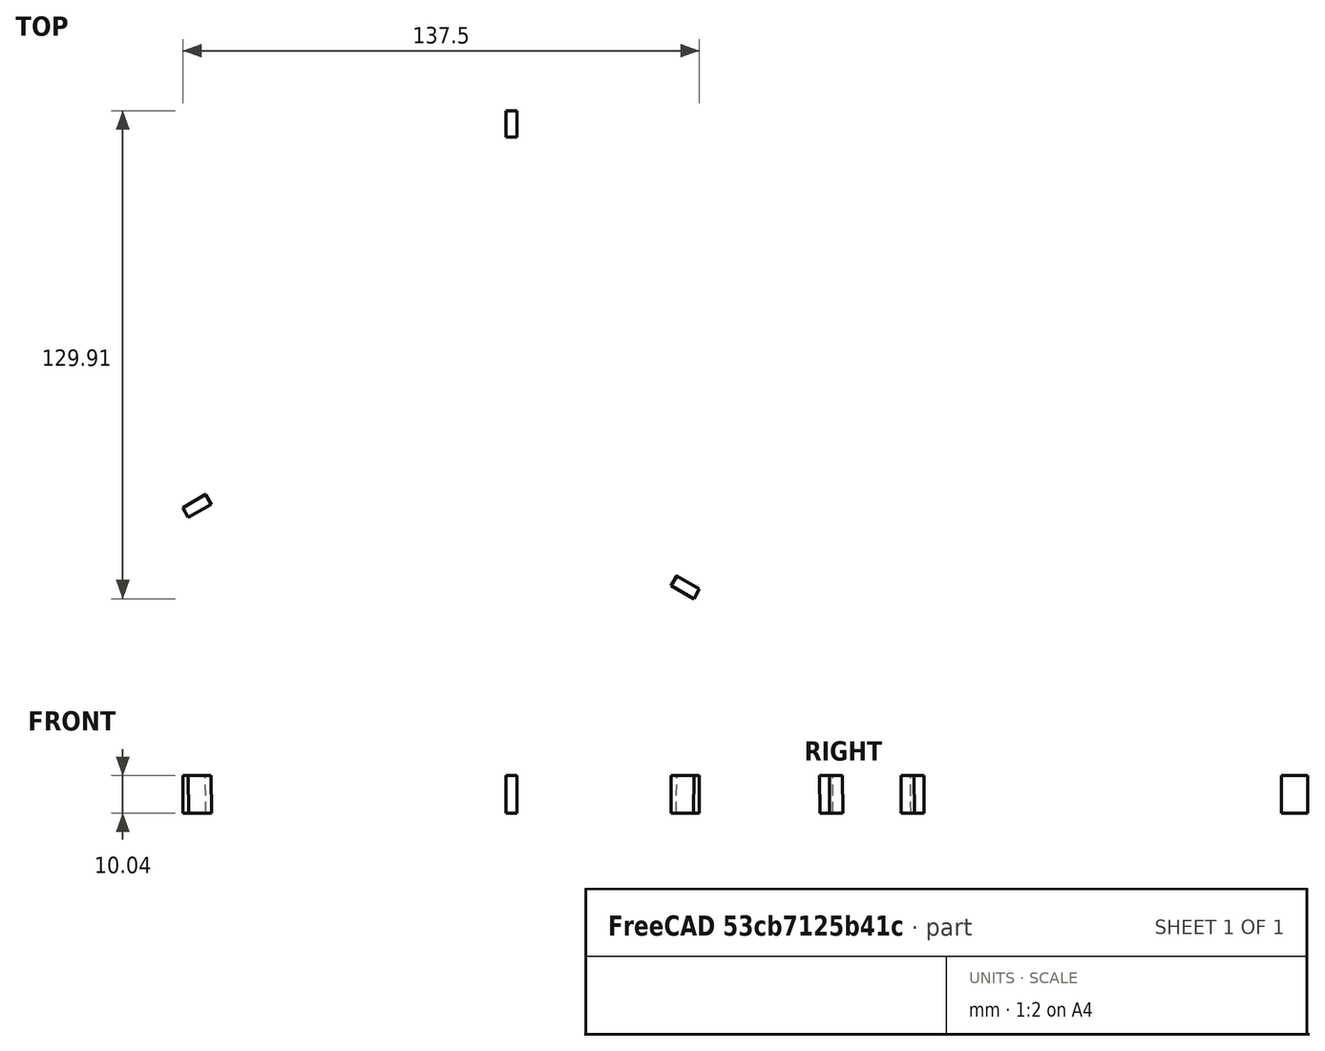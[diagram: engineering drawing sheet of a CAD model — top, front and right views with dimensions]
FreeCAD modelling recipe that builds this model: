
FCSTD DOCUMENT  (FreeCAD 2024.1R35694 (Git))
Label: deltarobot-example
License: All rights reserved
LicenseURL: http://en.wikipedia.org/wiki/All_rights_reserved
objects: App::FeaturePython×22, App::Link×17, Part::FeaturePython×3, Assembly::JointGroup×1, Assembly::AssemblyObject×1
note: 3 computed .brp shape members not serialized (recipe doc carries the construction recipe); baked Part::Feature solids carry a one-line shape summary decoded from their .brp
EXTERNAL_REF file=base.FCStd obj=Part
EXTERNAL_REF file=nema17-48.FCStd obj=Part
EXTERNAL_REF file=arm.FCStd obj=Part
EXTERNAL_REF file=plate.FCStd obj=Part
EXTERNAL_REF file=link.FCStd obj=Part
EXTERNAL_REF file=cone.FCStd obj=Part

FEATURE [App::Link] base  label="base 🔒"
  LinkedObject = -> <external base.FCStd>#Part
FEATURE [App::Link] nema17_48
  LinkPlacement = pos=(66.4519,-34.9019,1.93e-14) rot=(0.935113,-0.250563,-0.250563;1.63783rad)
  LinkedObject = -> <external nema17-48.FCStd>#Part
  Placement = pos=(66.4519,-34.9019,1.93e-14) rot=(0.935113,-0.250563,-0.250563;1.63783rad)
FEATURE [App::Link] nema17_049
  LinkPlacement = pos=(-63.4519,-40.0981,5.19e-14) rot=(-0.935113,-0.250563,0.250563;1.63783rad)
  LinkedObject = -> <external nema17-48.FCStd>#Part
  Placement = pos=(-63.4519,-40.0981,5.19e-14) rot=(-0.935113,-0.250563,0.250563;1.63783rad)
FEATURE [App::Link] nema17_050
  LinkPlacement = pos=(-3,75,4.4e-15) rot=(0.57735,-0.57735,0.57735;4.18879rad)
  LinkedObject = -> <external nema17-48.FCStd>#Part
  Placement = pos=(-3,75,4.4e-15) rot=(0.57735,-0.57735,0.57735;4.18879rad)
FEATURE [App::FeaturePython] GroundedJoint  # Assembly grounded joint (typed FeaturePython)
  ObjectToGround = -> base
FEATURE [App::FeaturePython] Fixed  # Assembly joint (typed FeaturePython)
  Detach1 = false
  Detach2 = false
  Distance = 0
  Element1 = Edge11
  Element2 = Edge27
  FirstPartConnected = false
  JointType = 0 (Fixed)
  Object1 = Body
  Object2 = Body002
  Offset = (0,0,0)
  Part1 = -> nema17_48
  Part2 = -> base
  Placement1 = pos=(0,0,48) rot=(0,0,1;0rad)
  Placement2 = pos=(67.4519,-33.1699,1.95e-14) rot=(0.935113,-0.250563,-0.250563;1.63783rad)
  Rotation = 0
  Vertex1 = Edge11
  Vertex2 = Edge27
FEATURE [App::FeaturePython] Fixed001  # Assembly joint (typed FeaturePython)
  Detach1 = false
  Detach2 = false
  Distance = 0
  Element1 = Edge11
  Element2 = Edge32
  FirstPartConnected = false
  JointType = 0 (Fixed)
  Object1 = Body
  Object2 = Body002
  Offset = (0,0,0)
  Part1 = -> nema17_049
  Part2 = -> base
  Placement1 = pos=(0,0,48) rot=(0,0,1;0rad)
  Placement2 = pos=(-62.4519,-41.8301,5.28e-14) rot=(-0.186157,0.694747,0.694747;3.50969rad)
  Rotation = 0
  Vertex1 = Edge11
  Vertex2 = Edge32
FEATURE [App::FeaturePython] Fixed002  # Assembly joint (typed FeaturePython)
  Detach1 = false
  Detach2 = false
  Distance = 0
  Element1 = Edge11
  Element2 = Edge12
  FirstPartConnected = false
  JointType = 0 (Fixed)
  Object1 = Body
  Object2 = Body002
  Offset = (0,0,0)
  Part1 = -> nema17_050
  Part2 = -> base
  Placement1 = pos=(0,0,48) rot=(0,0,1;0rad)
  Placement2 = pos=(-5,75,4.4e-15) rot=(0.57735,0.57735,0.57735;2.0944rad)
  Rotation = 0
  Vertex1 = Edge11
  Vertex2 = Edge12
FEATURE [App::Link] arm
  LinkPlacement = pos=(61.4519,-43.5622,1.88e-14) rot=(0.696382,-0.186595,0.69299;2.7744rad)
  LinkedObject = -> <external arm.FCStd>#Part
  Placement = pos=(61.4519,-43.5622,1.88e-14) rot=(0.696382,-0.186595,0.69299;2.7744rad)
FEATURE [App::Link] arm001
  LinkPlacement = pos=(-68.4519,-31.4378,4.74e-14) rot=(0.250639,-0.935398,0.249419;1.6424rad)
  LinkedObject = -> <external arm.FCStd>#Part
  Placement = pos=(-68.4519,-31.4378,4.74e-14) rot=(0.250639,-0.935398,0.249419;1.6424rad)
FEATURE [App::Link] arm002
  LinkPlacement = pos=(7,75,5.5e-15) rot=(0.578288,0.578288,0.575471;4.18597rad)
  LinkedObject = -> <external arm.FCStd>#Part
  Placement = pos=(7,75,5.5e-15) rot=(0.578288,0.578288,0.575471;4.18597rad)
FEATURE [App::FeaturePython] Revolute  # Assembly joint (typed FeaturePython)
  Detach1 = false
  Detach2 = false
  Distance = 0
  Element1 = Edge44
  Element2 = Edge38
  FirstPartConnected = true
  JointType = 1 (Revolute)
  Object1 = Body
  Object2 = Body001
  Offset = (0,0,0)
  Part1 = -> nema17_48
  Part2 = -> arm
  Placement1 = pos=(0,0,50) rot=(1,0,0;3.14159rad)
  Placement2 = pos=(0,-10,6.7e-15) rot=(1,0,0;1.5708rad)
  Rotation = 0
  Vertex1 = Edge44
  Vertex2 = Edge38
FEATURE [App::FeaturePython] Revolute001  # Assembly joint (typed FeaturePython)
  Detach1 = false
  Detach2 = false
  Distance = 0
  Element1 = Edge38
  Element2 = Edge44
  FirstPartConnected = false
  JointType = 1 (Revolute)
  Object1 = Body001
  Object2 = Body
  Offset = (0,0,0)
  Part1 = -> arm001
  Part2 = -> nema17_049
  Placement1 = pos=(0,-10,6.7e-15) rot=(1,0,0;1.5708rad)
  Placement2 = pos=(0,0,50) rot=(1,0,0;3.14159rad)
  Rotation = 0
  Vertex1 = Edge38
  Vertex2 = Edge44
FEATURE [App::FeaturePython] Revolute002  # Assembly joint (typed FeaturePython)
  Detach1 = false
  Detach2 = false
  Distance = 0
  Element1 = Edge38
  Element2 = Edge44
  FirstPartConnected = false
  JointType = 1 (Revolute)
  Object1 = Body001
  Object2 = Body
  Offset = (0,0,0)
  Part1 = -> arm002
  Part2 = -> nema17_050
  Placement1 = pos=(0,-10,6.7e-15) rot=(1,0,0;1.5708rad)
  Placement2 = pos=(0,0,50) rot=(1,0,0;3.14159rad)
  Rotation = 0
  Vertex1 = Edge38
  Vertex2 = Edge44
FEATURE [App::Link] plate
  LinkPlacement = pos=(8.1e-15,-1.46e-14,116) rot=(0,0,1;0rad)
  LinkedObject = -> <external plate.FCStd>#Part
  Placement = pos=(8.1e-15,-1.46e-14,116) rot=(0,0,1;0rad)
FEATURE [App::Link] link
  LinkPlacement = pos=(89.576,-22.8492,57.8706) rot=(-0.676617,0.713401,0.182342;1.52525rad)
  LinkedObject = -> <external link.FCStd>#Part
  Placement = pos=(89.576,-22.8492,57.8706) rot=(-0.676617,0.713401,0.182342;1.52525rad)
FEATURE [App::Link] link001
  LinkPlacement = pos=(64.576,-66.1505,57.8706) rot=(0.826476,0.110324,-0.552056;2.256rad)
  LinkedObject = -> <external link.FCStd>#Part
  Placement = pos=(64.576,-66.1505,57.8706) rot=(0.826476,0.110324,-0.552056;2.256rad)
FEATURE [App::Link] link002
  LinkPlacement = pos=(-64.576,-66.1505,57.8706) rot=(0.161974,0.81154,-0.561398;2.1205rad)
  LinkedObject = -> <external link.FCStd>#Part
  Placement = pos=(-64.576,-66.1505,57.8706) rot=(0.161974,0.81154,-0.561398;2.1205rad)
FEATURE [App::Link] link003
  LinkPlacement = pos=(-89.576,-22.8492,57.8706) rot=(-0.498673,0.455531,0.737439;2.90945rad)
  LinkedObject = -> <external link.FCStd>#Part
  Placement = pos=(-89.576,-22.8492,57.8706) rot=(-0.498673,0.455531,0.737439;2.90945rad)
FEATURE [App::Link] link004
  LinkPlacement = pos=(25,88.9997,57.8706) rot=(0.362835,0.914909,0.176894;1.72299rad)
  LinkedObject = -> <external link.FCStd>#Part
  Placement = pos=(25,88.9997,57.8706) rot=(0.362835,0.914909,0.176894;1.72299rad)
FEATURE [App::Link] link005
  LinkPlacement = pos=(-25,88.9997,57.8706) rot=(0.226144,-0.912799,-0.340083;1.62472rad)
  LinkedObject = -> <external link.FCStd>#Part
  Placement = pos=(-25,88.9997,57.8706) rot=(0.226144,-0.912799,-0.340083;1.62472rad)
FEATURE [App::FeaturePython] Ball  # Assembly joint (typed FeaturePython)
  Detach1 = false
  Detach2 = false
  Distance = 0
  Element1 = Face10
  Element2 = Face17
  FirstPartConnected = false
  JointType = 4 (Ball)
  Object1 = Body
  Object2 = Body001
  Offset = (0,0,0)
  Part1 = -> link
  Part2 = -> arm
  Placement1 = pos=(70,0,0) rot=(1,0,0;3.14159rad)
  Placement2 = pos=(0,-32,53) rot=(0.57735,0.57735,0.57735;4.18879rad)
  Rotation = 0
  Vertex1 = Face10
  Vertex2 = Face17
FEATURE [App::FeaturePython] Ball001  # Assembly joint (typed FeaturePython)
  Detach1 = false
  Detach2 = false
  Distance = 0
  Element1 = Face18
  Element2 = Face9
  FirstPartConnected = false
  JointType = 4 (Ball)
  Object1 = Body001
  Object2 = Body
  Offset = (0,0,0)
  Part1 = -> plate
  Part2 = -> link
  Placement1 = pos=(55.8013,-3.34936,0) rot=(0.935113,-0.250563,-0.250563;1.63783rad)
  Placement2 = pos=(-70,0,0) rot=(0,0,1;3.14159rad)
  Rotation = 0
  Vertex1 = Face18
  Vertex2 = Face9
FEATURE [App::FeaturePython] Ball002  # Assembly joint (typed FeaturePython)
  Detach1 = false
  Detach2 = false
  Distance = 0
  Element1 = Face18
  Element2 = Face10
  FirstPartConnected = true
  JointType = 4 (Ball)
  Object1 = Body001
  Object2 = Body
  Offset = (0,0,0)
  Part1 = -> arm
  Part2 = -> link001
  Placement1 = pos=(0,18,53) rot=(0.57735,0.57735,0.57735;4.18879rad)
  Placement2 = pos=(70,0,0) rot=(1,0,0;3.14159rad)
  Rotation = 0
  Vertex1 = Face18
  Vertex2 = Face10
FEATURE [App::FeaturePython] Ball003  # Assembly joint (typed FeaturePython)
  Detach1 = false
  Detach2 = false
  Distance = 0
  Element1 = Face9
  Element2 = Face17
  FirstPartConnected = true
  JointType = 4 (Ball)
  Object1 = Body
  Object2 = Body001
  Offset = (0,0,0)
  Part1 = -> link001
  Part2 = -> plate
  Placement1 = pos=(-70,0,0) rot=(0,0,1;3.14159rad)
  Placement2 = pos=(30.8013,-46.6506,0) rot=(0.935113,-0.250563,-0.250563;1.63783rad)
  Rotation = 0
  Vertex1 = Face9
  Vertex2 = Face17
FEATURE [App::FeaturePython] Ball004  # Assembly joint (typed FeaturePython)
  Detach1 = false
  Detach2 = false
  Distance = 0
  Element1 = Face17
  Element2 = Face10
  FirstPartConnected = true
  JointType = 4 (Ball)
  Object1 = Body001
  Object2 = Body
  Offset = (0,0,0)
  Part1 = -> arm001
  Part2 = -> link002
  Placement1 = pos=(0,-32,53) rot=(0.57735,0.57735,0.57735;4.18879rad)
  Placement2 = pos=(70,0,0) rot=(1,0,0;3.14159rad)
  Rotation = 0
  Vertex1 = Face17
  Vertex2 = Face10
FEATURE [App::FeaturePython] Ball005  # Assembly joint (typed FeaturePython)
  Detach1 = false
  Detach2 = false
  Distance = 0
  Element1 = Face18
  Element2 = Face10
  FirstPartConnected = true
  JointType = 4 (Ball)
  Object1 = Body001
  Object2 = Body
  Offset = (0,0,0)
  Part1 = -> arm001
  Part2 = -> link003
  Placement1 = pos=(0,18,53) rot=(0.57735,0.57735,0.57735;4.18879rad)
  Placement2 = pos=(70,0,0) rot=(1,0,0;3.14159rad)
  Rotation = 0
  Vertex1 = Face18
  Vertex2 = Face10
FEATURE [App::FeaturePython] Ball006  # Assembly joint (typed FeaturePython)
  Detach1 = false
  Detach2 = false
  Distance = 0
  Element1 = Face3
  Element2 = Face9
  FirstPartConnected = true
  JointType = 4 (Ball)
  Object1 = Body001
  Object2 = Body
  Offset = (0,0,0)
  Part1 = -> plate
  Part2 = -> link002
  Placement1 = pos=(-30.8013,-46.6506,0) rot=(-0.186157,0.694747,0.694747;3.50969rad)
  Placement2 = pos=(-70,0,0) rot=(0,0,1;3.14159rad)
  Rotation = 0
  Vertex1 = Face3
  Vertex2 = Face9
FEATURE [App::FeaturePython] Ball007  # Assembly joint (typed FeaturePython)
  Detach1 = false
  Detach2 = false
  Distance = 0
  Element1 = Face1
  Element2 = Face9
  FirstPartConnected = true
  JointType = 4 (Ball)
  Object1 = Body001
  Object2 = Body
  Offset = (0,0,0)
  Part1 = -> plate
  Part2 = -> link003
  Placement1 = pos=(-55.8013,-3.34936,0) rot=(-0.186157,0.694747,0.694747;3.50969rad)
  Placement2 = pos=(-70,0,0) rot=(0,0,1;3.14159rad)
  Rotation = 0
  Vertex1 = Face1
  Vertex2 = Face9
FEATURE [App::FeaturePython] Ball008  # Assembly joint (typed FeaturePython)
  Detach1 = false
  Detach2 = false
  Distance = 0
  Element1 = Face17
  Element2 = Face9
  FirstPartConnected = true
  JointType = 4 (Ball)
  Object1 = Body001
  Object2 = Body
  Offset = (0,0,0)
  Part1 = -> arm002
  Part2 = -> link005
  Placement1 = pos=(0,-32,53) rot=(0.57735,0.57735,0.57735;4.18879rad)
  Placement2 = pos=(-70,0,0) rot=(0,0,1;3.14159rad)
  Rotation = 0
  Vertex1 = Face17
  Vertex2 = Face9
FEATURE [App::FeaturePython] Ball009  # Assembly joint (typed FeaturePython)
  Detach1 = false
  Detach2 = false
  Distance = 0
  Element1 = Face16
  Element2 = Face10
  FirstPartConnected = true
  JointType = 4 (Ball)
  Object1 = Body001
  Object2 = Body
  Offset = (0,0,0)
  Part1 = -> plate
  Part2 = -> link005
  Placement1 = pos=(-25,50,0) rot=(0.57735,0.57735,0.57735;2.0944rad)
  Placement2 = pos=(70,0,0) rot=(1,0,0;3.14159rad)
  Rotation = 0
  Vertex1 = Face16
  Vertex2 = Face10
FEATURE [App::FeaturePython] Ball010  # Assembly joint (typed FeaturePython)
  Detach1 = false
  Detach2 = false
  Distance = 0
  Element1 = Face18
  Element2 = Face10
  FirstPartConnected = true
  JointType = 4 (Ball)
  Object1 = Body001
  Object2 = Body
  Offset = (0,0,0)
  Part1 = -> arm002
  Part2 = -> link004
  Placement1 = pos=(0,18,53) rot=(0.57735,0.57735,0.57735;4.18879rad)
  Placement2 = pos=(70,0,0) rot=(1,0,0;3.14159rad)
  Rotation = 0
  Vertex1 = Face18
  Vertex2 = Face10
FEATURE [App::FeaturePython] Ball011  # Assembly joint (typed FeaturePython)
  Detach1 = false
  Detach2 = false
  Distance = 0
  Element1 = Face15
  Element2 = Face9
  FirstPartConnected = true
  JointType = 4 (Ball)
  Object1 = Body001
  Object2 = Body
  Offset = (0,0,0)
  Part1 = -> plate
  Part2 = -> link004
  Placement1 = pos=(25,50,0) rot=(0.57735,0.57735,0.57735;2.0944rad)
  Placement2 = pos=(-70,0,0) rot=(0,0,1;3.14159rad)
  Rotation = 0
  Vertex1 = Face15
  Vertex2 = Face9
FEATURE [App::Link] cone
  LinkPlacement = pos=(7,107,-26) rot=(0,0,1;0rad)
  LinkedObject = -> <external cone.FCStd>#Part
  Placement = pos=(7,107,-26) rot=(0,0,1;0rad)
FEATURE [App::Link] cone001
  LinkPlacement = pos=(-96,-48,-26) rot=(0,0,1;0rad)
  LinkedObject = -> <external cone.FCStd>#Part
  Placement = pos=(-96,-48,-26) rot=(0,0,1;0rad)
FEATURE [App::Link] cone002
  LinkPlacement = pos=(92,-61,-26) rot=(0,0,1;0rad)
  LinkedObject = -> <external cone.FCStd>#Part
  Placement = pos=(92,-61,-26) rot=(0,0,1;0rad)
FEATURE [Part::FeaturePython] MotorObserver0  # WARN: FeaturePython — macro-defined, semantics opaque (R4)
  Enabled = true
  Placement = pos=(58.7019,-48.3253,1.82e-14) rot=(0.655971,0.376593,0.654125;3.86752rad)
  Reversed = true
  TransfAngle = 360
FEATURE [Part::FeaturePython] MotorObserver1  # WARN: FeaturePython — macro-defined, semantics opaque (R4)
  Enabled = true
  Placement = pos=(-71.2019,-26.6747,4.45e-14) rot=(0.653335,-0.379333,0.655179;2.42206rad)
  Reversed = true
  TransfAngle = 360
FEATURE [Part::FeaturePython] MotorObserver2  # WARN: FeaturePython — macro-defined, semantics opaque (R4)
  Enabled = true
  Placement = pos=(12.5,75,5.9e-15) rot=(-0.002441,-0.999994,0.002441;1.5708rad)
  Reversed = true
  TransfAngle = 360
FEATURE [App::FeaturePython] Fixed003  # Assembly joint (typed FeaturePython)
  Activated = true
  Detach1 = false
  Detach2 = false
  Distance = 0
  Element1 = Face6
  Element2 = Edge34
  JointType = 0 (Fixed)
  Object1 = MotorObserver0
  Object2 = Body001
  Offset = (0,0,0)
  Part1 = -> MotorObserver0
  Part2 = -> arm
  Placement1 = pos=(2e-16,0,1.5) rot=(0,0,1;0rad)
  Placement2 = pos=(0,4,-2.7e-15) rot=(1,0,0;1.5708rad)
  Rotation = 0
  Vertex1 = Face6
  Vertex2 = Edge34
FEATURE [App::FeaturePython] Fixed004  # Assembly joint (typed FeaturePython)
  Activated = true
  Detach1 = false
  Detach2 = false
  Distance = 0
  Element1 = Face6
  Element2 = Edge34
  JointType = 0 (Fixed)
  Object1 = MotorObserver1
  Object2 = Body001
  Offset = (0,0,0)
  Part1 = -> MotorObserver1
  Part2 = -> arm001
  Placement1 = pos=(3e-16,0,1.5) rot=(0,0,1;0rad)
  Placement2 = pos=(0,4,-2.7e-15) rot=(1,0,0;1.5708rad)
  Rotation = 0
  Vertex1 = Face6
  Vertex2 = Edge34
FEATURE [App::FeaturePython] Fixed005  # Assembly joint (typed FeaturePython)
  Activated = true
  Detach1 = false
  Detach2 = false
  Distance = 0
  Element1 = Face6
  Element2 = Edge34
  JointType = 0 (Fixed)
  Object1 = MotorObserver2
  Object2 = Body001
  Offset = (0,0,0)
  Part1 = -> MotorObserver2
  Part2 = -> arm002
  Placement1 = pos=(1e-16,0,1.5) rot=(0,0,1;0rad)
  Placement2 = pos=(0,4,-2.7e-15) rot=(1,0,0;1.5708rad)
  Rotation = 0
  Vertex1 = Face6
  Vertex2 = Edge34
FEATURE [Assembly::JointGroup] Joints
  Group = -> [GroundedJoint,Fixed,Fixed001,Fixed002,Revolute,Revolute001,Revolute002,Ball,Ball001,Ball002,Ball003,Ball004,Ball005,Ball006,Ball007,Ball008,Ball009,Ball010,Ball011,Fixed003,Fixed004,Fixed005]
FEATURE [Assembly::AssemblyObject] Assembly  label="deltabot"
  Group = -> [Joints,base,nema17_48,nema17_049,nema17_050,GroundedJoint,Fixed,Fixed001,Fixed002,arm,arm001,arm002,Revolute,Revolute001,Revolute002,plate,link,link001,link002,link003,link004,link005,Ball,Ball001,Ball002,Ball003,Ball004,Ball005,Ball006,Ball007,Ball008,Ball009,Ball010,Ball011,cone,cone001,cone002,MotorObserver0,MotorObserver1,MotorObserver2,Fixed003,Fixed004,Fixed005]
  Origin = -> Origin
  Type = Assembly

RESOLVED EXTERNAL PARTS (link-assembly join: the EXTERNAL_REF files above that resolve inside this repo's crawl, each included once):
---- part arm.FCStd = doc fcstd_cb6b5a2d1849 ----
FCSTD DOCUMENT  (FreeCAD 2024.1R35694 (Git))
Label: arm
License: All rights reserved
LicenseURL: http://en.wikipedia.org/wiki/All_rights_reserved
objects: Sketcher::SketchObject×11, PartDesign::Pad×6, PartDesign::Plane×2, PartDesign::Revolution×2, PartDesign::Mirrored×2, PartDesign::Body×2, PartDesign::Pocket×2, PartDesign::Chamfer×1, PartDesign::Hole×1, PartDesign::Fillet×1, App::Part×1
note: 43 computed .brp shape members not serialized (recipe doc carries the construction recipe); baked Part::Feature solids carry a one-line shape summary decoded from their .brp

FEATURE [PartDesign::Plane] DatumPlane002  label="midplane001"
  AttachmentOffset = pos=(0,0,7) rot=(0,0,1;0rad)
  Length = 60
  MapMode = 5
  Placement = pos=(0,-7,1.6e-15) rot=(1,0,0;1.5708rad)
  ResizeMode = 0
  Support = -> [XZ_Plane002]
  Width = 60
FEATURE [Sketcher::SketchObject] Sketch008
  FullyConstrained = true
  MapMode = 5
  Placement = pos=(0,0,0) rot=(1,0,0;1.5708rad)
  Support = -> [XZ_Plane002]
  sketch-geometry (5):
    g0: Circle CenterX=0 CenterY=0 CenterZ=0 NormalX=0 NormalY=0 NormalZ=1 AngleXU=0 Radius=2.5
    g1: ArcOfCircle CenterX=0 CenterY=0 CenterZ=0 NormalX=0 NormalY=0 NormalZ=1 AngleXU=0 Radius=6 StartAngle=3.14159 EndAngle=6.28319
    g2: LineSegment StartX=-6 StartY=-1.9e-15 StartZ=0 EndX=-6 EndY=50 EndZ=0
    g3: LineSegment StartX=6 StartY=-1.5e-15 StartZ=0 EndX=6 EndY=50 EndZ=0
    g4: LineSegment StartX=-6 StartY=50 StartZ=0 EndX=6 EndY=50 EndZ=0
  constraints (12):
    c: Coincident(g0,g-1)
    c: Tangent(g1,g2) = 1.5708
    c: Tangent(g1,g3) = -1.5708
    c: Vertical(g3)
    c: Diameter(g0) = 5
    c: Distance(g1,g1) = 12
    c: PointOnObject(g1,g-1)
    c: Coincident(g4,g2)
    c: Coincident(g4,g3)
    c: DistanceY(g3,g3) = 50
    c: Vertical(g2)
    c: Symmetric(g2,g3,g-2)
FEATURE [PartDesign::Pad] Pad003
  Direction = (0,-1,2e-16)
  Length = 8
  Length2 = 10
  Midplane = true
  Placement = pos=(0,0,0) rot=(1,0,0;1.5708rad)
  Profile = -> Sketch008
  ReferenceAxis = -> Sketch008 [N_Axis]
  Type = 0
FEATURE [Sketcher::SketchObject] Sketch009
  FullyConstrained = true
  MapMode = 5
  Placement = pos=(0,0,0) rot=(1,0,0;1.5708rad)
  Support = -> [XZ_Plane002]
  sketch-geometry (2):
    g0: Circle CenterX=0 CenterY=0 CenterZ=0 NormalX=0 NormalY=0 NormalZ=1 AngleXU=0 Radius=2.5
    g1: Circle CenterX=0 CenterY=0 CenterZ=0 NormalX=0 NormalY=0 NormalZ=1 AngleXU=0 Radius=6
  constraints (4):
    c: Coincident(g0,g-1)
    c: Coincident(g1,g0)
    c: Diameter(g0) = 5
    c: Diameter(g1) = 12
FEATURE [PartDesign::Pad] Pad004
  BaseFeature = -> Pad003
  Direction = (0,-1,2e-16)
  Length = 10
  Length2 = 10
  Placement = pos=(0,0,0) rot=(1,0,0;1.5708rad)
  Profile = -> Sketch009
  ReferenceAxis = -> Sketch009 [N_Axis]
  Refine = true
  Type = 0
FEATURE [Sketcher::SketchObject] Sketch010
  ExternalGeometry = -> [Pad004]
  FullyConstrained = true
  MapMode = 5
  Placement = pos=(0,-7,1.6e-15) rot=(1,0,0;1.5708rad)
  Support = -> [DatumPlane002]
  sketch-geometry (4):
    g0: LineSegment StartX=-6 StartY=50 StartZ=0 EndX=6 EndY=50 EndZ=0
    g1: LineSegment StartX=6 StartY=50 StartZ=0 EndX=6 EndY=56 EndZ=0
    g2: LineSegment StartX=6 StartY=56 StartZ=0 EndX=-6 EndY=56 EndZ=0
    g3: LineSegment StartX=-6 StartY=56 StartZ=0 EndX=-6 EndY=50 EndZ=0
  constraints (10):
    c: Coincident(g0,g1)
    c: Coincident(g1,g2)
    c: Coincident(g2,g3)
    c: Coincident(g3,g0)
    c: Horizontal(g2)
    c: Vertical(g1)
    c: Vertical(g3)
    c: Coincident(g0,g-3)
    c: Coincident(g0,g-3)
    c: DistanceY(g1,g1) = 6
FEATURE [PartDesign::Pad] Pad005
  BaseFeature = -> Pad004
  Direction = (0,-1,2e-16)
  Length = 36
  Length2 = 10
  Midplane = true
  Placement = pos=(0,0,0) rot=(1,0,0;1.5708rad)
  Profile = -> Sketch010
  ReferenceAxis = -> Sketch010 [N_Axis]
  Refine = true
  Type = 0
FEATURE [Sketcher::SketchObject] Sketch011
  ExternalGeometry = -> [Pad005,DatumPlane002]
  FullyConstrained = true
  MapMode = 5
  Placement = pos=(0,0,0) rot=(0.57735,0.57735,0.57735;2.0944rad)
  Support = -> [YZ_Plane002]
  sketch-geometry (4):
    g0: LineSegment StartX=-37 StartY=53 StartZ=0 EndX=-25 EndY=53 EndZ=0
    g1: ArcOfCircle CenterX=-32 CenterY=53 CenterZ=0 NormalX=0 NormalY=0 NormalZ=1 AngleXU=0 Radius=5 StartAngle=0.643501 EndAngle=3.14159
    g2: LineSegment StartX=-28 StartY=56 StartZ=0 EndX=-25 EndY=56 EndZ=0
    g3: LineSegment StartX=-25 StartY=56 StartZ=0 EndX=-25 EndY=53 EndZ=0
  constraints (12):
    c: Symmetric(g-3,g-3,g0)
    c: PointOnObject(g1,g0)
    c: Coincident(g1,g0)
    c: PointOnObject(g0,g-3)
    c: Radius(g1) = 5
    c: Distance(g1,g-4) = 25
    c: Coincident(g1,g2)
    c: PointOnObject(g2,g-3)
    c: Horizontal(g2)
    c: Coincident(g2,g3)
    c: Coincident(g3,g0)
    c: DistanceY(g0,g2) = 3
FEATURE [PartDesign::Revolution] Revolution
  Angle = 360
  Angle2 = 60
  Axis = (0,1,0)
  Base = (0,-37,53)
  BaseFeature = -> Pad005
  Placement = pos=(0,0,0) rot=(1,0,0;1.5708rad)
  Profile = -> Sketch011
  ReferenceAxis = -> Sketch011 [Edge1]
  Refine = true
  Type = 0
FEATURE [PartDesign::Mirrored] Mirrored002
  BaseFeature = -> Revolution
  MirrorPlane = -> DatumPlane002
  Originals = -> [Revolution]
  Placement = pos=(0,0,0) rot=(1,0,0;1.5708rad)
  Refine = true
FEATURE [PartDesign::Body] Body001  label="arm-skeleton"
  Group = -> [Sketch008,Pad003,Sketch009,Pad004,DatumPlane002,Sketch010,Pad005,Sketch011,Revolution,Mirrored002]
  Origin = -> Origin002
  Tip = -> Mirrored002
FEATURE [PartDesign::Plane] DatumPlane003  label="midplane002"
  AttachmentOffset = pos=(0,0,7) rot=(0,0,1;0rad)
  Length = 60
  MapMode = 5
  Placement = pos=(0,-7,1.6e-15) rot=(1,0,0;1.5708rad)
  ResizeMode = 0
  Support = -> [XZ_Plane002]
  Width = 60
FEATURE [Sketcher::SketchObject] Sketch012
  FullyConstrained = true
  MapMode = 5
  Placement = pos=(0,0,0) rot=(1,0,0;1.5708rad)
  Support = -> [XZ_Plane003]
  sketch-geometry (5):
    g0: Circle CenterX=0 CenterY=0 CenterZ=0 NormalX=0 NormalY=0 NormalZ=1 AngleXU=0 Radius=2.5
    g1: ArcOfCircle CenterX=0 CenterY=0 CenterZ=0 NormalX=0 NormalY=0 NormalZ=1 AngleXU=0 Radius=6 StartAngle=3.14159 EndAngle=6.28319
    g2: LineSegment StartX=-6 StartY=-1.9e-15 StartZ=0 EndX=-6 EndY=50 EndZ=0
    g3: LineSegment StartX=6 StartY=-1.5e-15 StartZ=0 EndX=6 EndY=50 EndZ=0
    g4: LineSegment StartX=-6 StartY=50 StartZ=0 EndX=6 EndY=50 EndZ=0
  constraints (12):
    c: Coincident(g0,g-1)
    c: Tangent(g1,g2) = 1.5708
    c: Tangent(g1,g3) = -1.5708
    c: Vertical(g3)
    c: Diameter(g0) = 5
    c: Distance(g1,g1) = 12
    c: PointOnObject(g1,g-1)
    c: Coincident(g4,g2)
    c: Coincident(g4,g3)
    c: DistanceY(g3,g3) = 50
    c: Vertical(g2)
    c: Symmetric(g2,g3,g-2)
FEATURE [PartDesign::Pad] Pad006
  Direction = (0,-1,2e-16)
  Length = 8
  Length2 = 10
  Midplane = true
  Placement = pos=(0,0,0) rot=(1,0,0;1.5708rad)
  Profile = -> Sketch012
  ReferenceAxis = -> Sketch012 [N_Axis]
  Type = 0
FEATURE [Sketcher::SketchObject] Sketch013
  FullyConstrained = true
  MapMode = 5
  Placement = pos=(0,0,0) rot=(1,0,0;1.5708rad)
  Support = -> [XZ_Plane003]
  sketch-geometry (2):
    g0: Circle CenterX=0 CenterY=0 CenterZ=0 NormalX=0 NormalY=0 NormalZ=1 AngleXU=0 Radius=2.5
    g1: Circle CenterX=0 CenterY=0 CenterZ=0 NormalX=0 NormalY=0 NormalZ=1 AngleXU=0 Radius=6
  constraints (4):
    c: Coincident(g0,g-1)
    c: Coincident(g1,g0)
    c: Diameter(g0) = 5
    c: Diameter(g1) = 12
FEATURE [PartDesign::Pad] Pad007
  BaseFeature = -> Pad006
  Direction = (0,-1,2e-16)
  Length = 10
  Length2 = 10
  Placement = pos=(0,0,0) rot=(1,0,0;1.5708rad)
  Profile = -> Sketch013
  ReferenceAxis = -> Sketch013 [N_Axis]
  Refine = true
  Type = 0
FEATURE [Sketcher::SketchObject] Sketch014
  ExternalGeometry = -> [Pad007]
  FullyConstrained = true
  MapMode = 5
  Placement = pos=(0,-7,1.6e-15) rot=(1,0,0;1.5708rad)
  Support = -> [DatumPlane003]
  sketch-geometry (4):
    g0: LineSegment StartX=-6 StartY=50 StartZ=0 EndX=6 EndY=50 EndZ=0
    g1: LineSegment StartX=6 StartY=50 StartZ=0 EndX=6 EndY=56 EndZ=0
    g2: LineSegment StartX=6 StartY=56 StartZ=0 EndX=-6 EndY=56 EndZ=0
    g3: LineSegment StartX=-6 StartY=56 StartZ=0 EndX=-6 EndY=50 EndZ=0
  constraints (10):
    c: Coincident(g0,g1)
    c: Coincident(g1,g2)
    c: Coincident(g2,g3)
    c: Coincident(g3,g0)
    c: Horizontal(g2)
    c: Vertical(g1)
    c: Vertical(g3)
    c: Coincident(g0,g-3)
    c: Coincident(g0,g-3)
    c: DistanceY(g1,g1) = 6
FEATURE [PartDesign::Pad] Pad008
  BaseFeature = -> Pad007
  Direction = (0,-1,2e-16)
  Length = 36
  Length2 = 10
  Midplane = true
  Placement = pos=(0,0,0) rot=(1,0,0;1.5708rad)
  Profile = -> Sketch014
  ReferenceAxis = -> Sketch014 [N_Axis]
  Refine = true
  Type = 0
FEATURE [Sketcher::SketchObject] Sketch015
  ExternalGeometry = -> [Pad008,DatumPlane003]
  FullyConstrained = true
  MapMode = 5
  Placement = pos=(0,0,0) rot=(0.57735,0.57735,0.57735;2.0944rad)
  Support = -> [YZ_Plane003]
  sketch-geometry (4):
    g0: LineSegment StartX=-36.9 StartY=53 StartZ=0 EndX=-25 EndY=53 EndZ=0
    g1: ArcOfCircle CenterX=-32 CenterY=53 CenterZ=0 NormalX=0 NormalY=0 NormalZ=1 AngleXU=0 Radius=4.9 StartAngle=0.658897 EndAngle=3.14159
    g2: LineSegment StartX=-28.1257 StartY=56 StartZ=0 EndX=-25 EndY=56 EndZ=0
    g3: LineSegment StartX=-25 StartY=56 StartZ=0 EndX=-25 EndY=53 EndZ=0
  constraints (12):
    c: Symmetric(g-3,g-3,g0)
    c: PointOnObject(g1,g0)
    c: Coincident(g1,g0)
    c: PointOnObject(g0,g-3)
    c: Radius(g1) = 4.9
    c: Distance(g1,g-4) = 25
    c: Coincident(g1,g2)
    c: PointOnObject(g2,g-3)
    c: Horizontal(g2)
    c: Coincident(g2,g3)
    c: Coincident(g3,g0)
    c: DistanceY(g0,g2) = 3
FEATURE [PartDesign::Revolution] Revolution001
  Angle = 360
  Angle2 = 60
  Axis = (0,1,0)
  Base = (0,-36.9,53)
  BaseFeature = -> Pad008
  Placement = pos=(0,0,0) rot=(1,0,0;1.5708rad)
  Profile = -> Sketch015
  ReferenceAxis = -> Sketch015 [Edge1]
  Refine = true
  Type = 0
FEATURE [PartDesign::Mirrored] Mirrored003
  BaseFeature = -> Revolution001
  MirrorPlane = -> DatumPlane003
  Originals = -> [Revolution001]
  Placement = pos=(0,0,0) rot=(1,0,0;1.5708rad)
  Refine = true
FEATURE [PartDesign::Chamfer] Chamfer
  Angle = 45
  Base = -> Mirrored003 [Edge12,Edge10,Edge17,Edge21]
  BaseFeature = -> Mirrored003
  ChamferType = 0
  FlipDirection = false
  Placement = pos=(0,0,0) rot=(1,0,0;1.5708rad)
  Refine = true
  Size = 2
  Size2 = 1
  SupportTransform = false
  UseAllEdges = false
FEATURE [Sketcher::SketchObject] Sketch
  FullyConstrained = true
  MapMode = 5
  Placement = pos=(0,0,0) rot=(1,0,0;1.5708rad)
  Support = -> [XZ_Plane003]
  sketch-geometry (4):
    g0: LineSegment StartX=0.5 StartY=0 StartZ=0 EndX=0.5 EndY=10 EndZ=0
    g1: LineSegment StartX=0.5 StartY=10 StartZ=0 EndX=-0.5 EndY=10 EndZ=0
    g2: LineSegment StartX=-0.5 StartY=10 StartZ=0 EndX=-0.5 EndY=0 EndZ=0
    g3: LineSegment StartX=-0.5 StartY=0 StartZ=0 EndX=0.5 EndY=0 EndZ=0
  constraints (11):
    c: Coincident(g0,g1)
    c: Coincident(g1,g2)
    c: Coincident(g2,g3)
    c: Coincident(g3,g0)
    c: Vertical(g0)
    c: Vertical(g2)
    c: Horizontal(g1)
    c: Horizontal(g3)
    c: Symmetric(g2,g0,g-1)
    c: Distance(g1,g1) = 1
    c: DistanceY(g0,g0) = 10
FEATURE [PartDesign::Pocket] Pocket
  BaseFeature = -> Chamfer
  Direction = (0,1,-2e-16)
  Length = 5
  Length2 = 5
  Midplane = true
  Placement = pos=(0,0,0) rot=(1,0,0;1.5708rad)
  Profile = -> Sketch
  ReferenceAxis = -> Sketch [N_Axis]
  Refine = true
  Type = 1
FEATURE [Sketcher::SketchObject] Sketch016
  FullyConstrained = true
  MapMode = 5
  Placement = pos=(6,0,0) rot=(0.707107,0,0.707107;3.14159rad)
  Support = -> [Pocket]
  sketch-geometry (1):
    g0: Circle CenterX=5 CenterY=0 CenterZ=0 NormalX=0 NormalY=0 NormalZ=1 AngleXU=0 Radius=1.5
  constraints (3):
    c: PointOnObject(g0,g-1)
    c: Diameter(g0) = 3
    c: DistanceX(g-1,g0) = 5
FEATURE [PartDesign::Hole] Hole
  BaseFeature = -> Pocket
  CustomThreadClearance = 0
  Depth = 178.805
  DepthType = 1
  Diameter = 3.4
  DrillForDepth = false
  DrillPoint = 1
  DrillPointAngle = 118
  HoleCutCountersinkAngle = 90
  HoleCutCustomValues = false
  HoleCutDepth = 0
  HoleCutDiameter = 6.1
  HoleCutType = 0
  ModelThread = false
  Placement = pos=(0,0,0) rot=(1,0,0;1.5708rad)
  Profile = -> Sketch016
  Refine = true
  Tapered = false
  TaperedAngle = 90
  ThreadClass = 0
  ThreadDepth = 178.805
  ThreadDepthType = 0
  ThreadDirection = 0
  ThreadFit = 0
  ThreadSize = 9
  ThreadType = 1
  Threaded = false
  UseCustomThreadClearance = false
FEATURE [Sketcher::SketchObject] Sketch017
  ExternalGeometry = -> [Hole]
  FullyConstrained = true
  MapMode = 5
  Placement = pos=(-6,0,0) rot=(0.707107,0,-0.707107;3.14159rad)
  Support = -> [Hole]
  sketch-geometry (7):
    g0: LineSegment StartX=-1.5359 StartY=-4e-16 StartZ=0 EndX=-3.26795 EndY=3 EndZ=0
    g1: LineSegment StartX=-3.26795 StartY=3 StartZ=0 EndX=-6.73205 EndY=3 EndZ=0
    g2: LineSegment StartX=-6.73205 StartY=3 StartZ=0 EndX=-8.4641 EndY=-9e-16 EndZ=0
    g3: LineSegment StartX=-8.4641 StartY=-9e-16 StartZ=0 EndX=-6.73205 EndY=-3 EndZ=0
    g4: LineSegment StartX=-6.73205 StartY=-3 StartZ=0 EndX=-3.26795 EndY=-3 EndZ=0
    g5: LineSegment StartX=-3.26795 StartY=-3 StartZ=0 EndX=-1.5359 EndY=-4e-16 EndZ=0
    g6: Circle CenterX=-5 CenterY=-6e-16 CenterZ=0 NormalX=0 NormalY=0 NormalZ=1 AngleXU=0 Radius=3.4641
  constraints (16):
    c: Coincident(g0,g1)
    c: Coincident(g1,g2)
    c: Coincident(g2,g3)
    c: Coincident(g3,g4)
    c: Coincident(g4,g5)
    c: Coincident(g5,g0)
    c: Equal(g0, g1-g5) x5
    c: PointOnObject(g0,g6)
    c: PointOnObject(g1,g6)
    c: PointOnObject(g2,g6)
    c: PointOnObject(g3,g6)
    c: PointOnObject(g4,g6)
    c: PointOnObject(g5,g6)
    c: Coincident(g6,g-3)
    c: DistanceY(g4,g0) = 6
    c: Horizontal(g1)
FEATURE [PartDesign::Pocket] Pocket001
  BaseFeature = -> Hole
  Direction = (1,0,2e-16)
  Length = 3
  Length2 = 5
  Placement = pos=(0,0,0) rot=(1,0,0;1.5708rad)
  Profile = -> Sketch017
  ReferenceAxis = -> Sketch017 [N_Axis]
  Refine = true
  Type = 0
FEATURE [PartDesign::Fillet] Fillet
  Base = -> Pocket001 [Edge3,Edge46]
  BaseFeature = -> Pocket001
  Placement = pos=(0,0,0) rot=(1,0,0;1.5708rad)
  Radius = 2
  Refine = true
  SupportTransform = false
  UseAllEdges = false
FEATURE [PartDesign::Body] Body002  label="arm0"
  Group = -> [Sketch012,Pad006,Sketch013,Pad007,DatumPlane003,Sketch014,Pad008,Sketch015,Revolution001,Mirrored003,Chamfer,Sketch,Pocket,Sketch016,Hole,Sketch017,Pocket001,Fillet]
  Origin = -> Origin003
  Tip = -> Fillet
FEATURE [App::Part] Part  label="arm"
  Group = -> [Body001,Body002]
  Origin = -> Origin
---- part base.FCStd = doc fcstd_4bb8bb395458 ----
FCSTD DOCUMENT  (FreeCAD 0.22R35451 (Git))
Label: base
License: All rights reserved
LicenseURL: http://en.wikipedia.org/wiki/All_rights_reserved
objects: Sketcher::SketchObject×7, PartDesign::Pad×5, PartDesign::Plane×4, PartDesign::PolarPattern×3, PartDesign::Body×2, PartDesign::Hole×1, PartDesign::Pocket×1, App::Part×1
note: 30 computed .brp shape members not serialized (recipe doc carries the construction recipe); baked Part::Feature solids carry a one-line shape summary decoded from their .brp

FEATURE [PartDesign::Plane] DatumPlane
  Length = 60
  MapMode = 5
  Placement = pos=(0,0,0) rot=(0.57735,0.57735,0.57735;2.0944rad)
  ResizeMode = 0
  Support = -> [YZ_Plane002]
  Width = 60
FEATURE [Sketcher::SketchObject] Sketch001
  FullyConstrained = true
  MapMode = 5
  Placement = pos=(0,0,0) rot=(0.57735,0.57735,0.57735;2.0944rad)
  Support = -> [DatumPlane]
  sketch-geometry (5):
    g0: Circle CenterX=75 CenterY=0 CenterZ=0 NormalX=0 NormalY=0 NormalZ=1 AngleXU=0 Radius=11.25
    g1: LineSegment StartX=96 StartY=21 StartZ=0 EndX=0 EndY=21 EndZ=0
    g2: LineSegment StartX=0 StartY=21 StartZ=0 EndX=0 EndY=-26 EndZ=0
    g3: LineSegment StartX=0 StartY=-26 StartZ=0 EndX=96 EndY=-26 EndZ=0
    g4: LineSegment StartX=96 StartY=-26 StartZ=0 EndX=96 EndY=21 EndZ=0
  constraints (15):
    c: PointOnObject(g0,g-1)
    c: Diameter(g0) = 22.5
    c: DistanceX(g-1,g0) = 75
    c: Coincident(g1,g2)
    c: Coincident(g2,g3)
    c: Coincident(g3,g4)
    c: Coincident(g4,g1)
    c: Horizontal(g1)
    c: Horizontal(g3)
    c: Vertical(g2)
    c: PointOnObject(g2,g-2)
    c: DistanceX(g0,g1) = 21
    c: DistanceY(g-1,g1) = 21
    c: DistanceY(g3,g-1) = 26
    c: Vertical(g4)
FEATURE [PartDesign::Pad] Pad001
  Direction = (1,0,0)
  Length = 5
  Length2 = 10
  Placement = pos=(0,0,0) rot=(0.57735,0.57735,0.57735;2.0944rad)
  Profile = -> Sketch001
  ReferenceAxis = -> Sketch001 [N_Axis]
  Reversed = true
  Type = 0
FEATURE [Sketcher::SketchObject] Sketch002
  ExternalGeometry = -> [Pad001]
  FullyConstrained = true
  MapMode = 5
  Placement = pos=(0,0,0) rot=(0.57735,0.57735,0.57735;2.0944rad)
  Support = -> [Pad001]
  sketch-geometry (5):
    g0: Circle CenterX=90.5 CenterY=15.5 CenterZ=0 NormalX=0 NormalY=0 NormalZ=1 AngleXU=0 Radius=2
    g1: LineSegment StartX=75 StartY=0 StartZ=0 EndX=75 EndY=11.25 EndZ=0
    g2: Circle CenterX=90.5 CenterY=-15.5 CenterZ=0 NormalX=0 NormalY=0 NormalZ=1 AngleXU=0 Radius=2
    g3: Circle CenterX=59.5 CenterY=-15.5 CenterZ=0 NormalX=0 NormalY=0 NormalZ=1 AngleXU=0 Radius=2
    g4: Circle CenterX=59.5 CenterY=15.5 CenterZ=0 NormalX=0 NormalY=0 NormalZ=1 AngleXU=0 Radius=2
  constraints (12):
    c: Coincident(g1,g-3)
    c: PointOnObject(g1,g-3)
    c: Vertical(g1)
    c: Symmetric(g0,g4,g1)
    c: Symmetric(g0,g2,g-1)
    c: Symmetric(g2,g3,g1)
    c: Equal(g4,g0)
    c: Equal(g0,g2)
    c: Equal(g2,g3)
    c: DistanceX(g4,g0) = 31
    c: DistanceY(g2,g0) = 31
    c: Diameter(g0) = 4
FEATURE [PartDesign::Hole] Hole
  BaseFeature = -> Pad001
  CustomThreadClearance = 0
  Depth = 25
  DepthType = 0
  Diameter = 3.4
  DrillForDepth = false
  DrillPoint = 1
  DrillPointAngle = 118
  HoleCutCountersinkAngle = 90
  HoleCutCustomValues = false
  HoleCutDepth = 3.4
  HoleCutDiameter = 6.1
  HoleCutType = 1
  ModelThread = false
  Placement = pos=(0,0,0) rot=(0.57735,0.57735,0.57735;2.0944rad)
  Profile = -> Sketch002
  Tapered = false
  TaperedAngle = 90
  ThreadClass = 0
  ThreadDepth = 25
  ThreadDepthType = 0
  ThreadDirection = 0
  ThreadFit = 0
  ThreadSize = 9
  ThreadType = 1
  Threaded = false
  UseCustomThreadClearance = false
FEATURE [PartDesign::Plane] DatumPlane001
  Length = 60
  MapMode = 5
  Placement = pos=(2.9e-15,0,-26) rot=(0.707107,0.707107,0;3.14159rad)
  ResizeMode = 0
  Support = -> [Pad001]
  Width = 60
FEATURE [Sketcher::SketchObject] Sketch003
  FullyConstrained = true
  MapMode = 5
  Placement = pos=(2.9e-15,0,-26) rot=(0.707107,0.707107,0;3.14159rad)
  Support = -> [DatumPlane001]
  sketch-geometry (1):
    g0: Circle CenterX=0 CenterY=0 CenterZ=0 NormalX=0 NormalY=0 NormalZ=1 AngleXU=0 Radius=5
  constraints (2):
    c: Coincident(g0,g-1)
    c: Diameter(g0) = 10
FEATURE [PartDesign::Pad] Pad002
  BaseFeature = -> Hole
  Direction = (0,0,-1)
  Length = 42
  Length2 = 10
  Placement = pos=(0,0,0) rot=(0.57735,0.57735,0.57735;2.0944rad)
  Profile = -> Sketch003
  ReferenceAxis = -> Sketch003 [N_Axis]
  Refine = true
  Reversed = true
  Type = 1
FEATURE [PartDesign::PolarPattern] PolarPattern
  Angle = 360
  Axis = -> Z_Axis002
  BaseFeature = -> Pad002
  Mode = 0
  Occurrences = 3
  Offset = 120
  Originals = -> [Pad001,Hole]
  Placement = pos=(0,0,0) rot=(0.57735,0.57735,0.57735;2.0944rad)
  Refine = true
FEATURE [Sketcher::SketchObject] Sketch
  FullyConstrained = true
  MapMode = 5
  Placement = pos=(2.9e-15,0,-26) rot=(0.707107,0.707107,0;3.14159rad)
  Support = -> [DatumPlane001]
  sketch-geometry (8):
    g0: LineSegment StartX=96 StartY=0 StartZ=0 EndX=-48 EndY=83.1384 EndZ=0
    g1: LineSegment StartX=-48 StartY=83.1384 StartZ=0 EndX=-48 EndY=-83.1384 EndZ=0
    g2: LineSegment StartX=-48 StartY=-83.1384 StartZ=0 EndX=96 EndY=0 EndZ=0
    g3: Circle CenterX=0 CenterY=0 CenterZ=0 NormalX=0 NormalY=0 NormalZ=1 AngleXU=0 Radius=96
    g4: LineSegment StartX=60 StartY=0 StartZ=0 EndX=-30 EndY=51.9615 EndZ=0
    g5: LineSegment StartX=-30 StartY=51.9615 StartZ=0 EndX=-30 EndY=-51.9615 EndZ=0
    g6: LineSegment StartX=-30 StartY=-51.9615 StartZ=0 EndX=60 EndY=0 EndZ=0
    g7: Circle CenterX=0 CenterY=0 CenterZ=0 NormalX=0 NormalY=0 NormalZ=1 AngleXU=0 Radius=60
  constraints (22):
    c: Coincident(g0,g1)
    c: Coincident(g1,g2)
    c: Coincident(g2,g0)
    c: Equal(g0,g1)
    c: Equal(g0,g2)
    c: PointOnObject(g0,g3)
    c: PointOnObject(g1,g3)
    c: PointOnObject(g2,g3)
    c: Coincident(g3,g-1)
    c: PointOnObject(g2,g-1)
    c: Coincident(g4,g5)
    c: Coincident(g5,g6)
    c: Coincident(g6,g4)
    c: Equal(g4,g5)
    c: Equal(g4,g6)
    c: PointOnObject(g4,g7)
    c: PointOnObject(g5,g7)
    c: PointOnObject(g6,g7)
    c: Coincident(g7,g3)
    c: PointOnObject(g6,g-1)
    c: DistanceX(g-1,g0) = 96
    c: DistanceX(g-1,g4) = 60
FEATURE [PartDesign::Pad] Pad
  BaseFeature = -> PolarPattern
  Direction = (0,0,-1)
  Length = 4
  Length2 = 10
  Placement = pos=(0,0,0) rot=(0.57735,0.57735,0.57735;2.0944rad)
  Profile = -> Sketch
  ReferenceAxis = -> Sketch [N_Axis]
  Refine = true
  Reversed = true
  Type = 0
FEATURE [Sketcher::SketchObject] Sketch004
  ExternalGeometry = -> [Pad]
  FullyConstrained = true
  MapMode = 5
  Placement = pos=(0,0,0) rot=(0.57735,0.57735,0.57735;2.0944rad)
  Support = -> [YZ_Plane002]
  sketch-geometry (4):
    g0: LineSegment StartX=82 StartY=21 StartZ=0 EndX=68 EndY=21 EndZ=0
    g1: LineSegment StartX=68 StartY=21 StartZ=0 EndX=68 EndY=8.80696 EndZ=0
    g2: LineSegment StartX=68 StartY=8.80696 StartZ=0 EndX=82 EndY=8.80696 EndZ=0
    g3: LineSegment StartX=82 StartY=8.80696 StartZ=0 EndX=82 EndY=21 EndZ=0
  constraints (12):
    c: Coincident(g0,g1)
    c: Coincident(g1,g2)
    c: Coincident(g2,g3)
    c: Coincident(g3,g0)
    c: Horizontal(g0)
    c: Horizontal(g2)
    c: Vertical(g1)
    c: Vertical(g3)
    c: PointOnObject(g0,g-4)
    c: PointOnObject(g1,g-3)
    c: PointOnObject(g2,g-3)
    c: DistanceX(g0,g0) = 14
FEATURE [PartDesign::Pocket] Pocket
  BaseFeature = -> Pad
  Direction = (-1,0,0)
  Length = 5
  Length2 = 5
  Placement = pos=(0,0,0) rot=(0.57735,0.57735,0.57735;2.0944rad)
  Profile = -> Sketch004
  ReferenceAxis = -> Sketch004 [N_Axis]
  Refine = true
  Type = 0
FEATURE [PartDesign::PolarPattern] PolarPattern001
  Angle = 360
  Axis = -> Z_Axis002
  BaseFeature = -> Pocket
  Mode = 0
  Occurrences = 3
  Offset = 120
  Originals = -> [Pocket]
  Placement = pos=(0,0,0) rot=(0.57735,0.57735,0.57735;2.0944rad)
  Refine = true
FEATURE [PartDesign::Body] Body001  label="base0"
  Group = -> [DatumPlane,Sketch001,Pad001,DatumPlane001,Sketch002,Hole,Sketch003,Pad002,PolarPattern,Sketch,Pad,Sketch004,Pocket,PolarPattern001]
  Origin = -> Origin002
  Tip = -> PolarPattern001
FEATURE [PartDesign::Plane] DatumPlane002
  Length = 60
  MapMode = 5
  Placement = pos=(0,0,0) rot=(0.57735,0.57735,0.57735;2.0944rad)
  ResizeMode = 0
  Support = -> [YZ_Plane003]
  Width = 60
FEATURE [Sketcher::SketchObject] Sketch006
  FullyConstrained = true
  MapMode = 5
  Placement = pos=(0,0,0) rot=(0.57735,0.57735,0.57735;2.0944rad)
  Support = -> [DatumPlane002]
  sketch-geometry (5):
    g0: Circle CenterX=75 CenterY=0 CenterZ=0 NormalX=0 NormalY=0 NormalZ=1 AngleXU=0 Radius=11.25
    g1: LineSegment StartX=96 StartY=21 StartZ=0 EndX=0 EndY=21 EndZ=0
    g2: LineSegment StartX=0 StartY=21 StartZ=0 EndX=0 EndY=-26 EndZ=0
    g3: LineSegment StartX=0 StartY=-26 StartZ=0 EndX=96 EndY=-26 EndZ=0
    g4: LineSegment StartX=96 StartY=-26 StartZ=0 EndX=96 EndY=21 EndZ=0
  constraints (15):
    c: PointOnObject(g0,g-1)
    c: Diameter(g0) = 22.5
    c: DistanceX(g-1,g0) = 75
    c: Coincident(g1,g2)
    c: Coincident(g2,g3)
    c: Coincident(g3,g4)
    c: Coincident(g4,g1)
    c: Horizontal(g1)
    c: Horizontal(g3)
    c: Vertical(g2)
    c: PointOnObject(g2,g-2)
    c: DistanceX(g0,g1) = 21
    c: DistanceY(g-1,g1) = 21
    c: DistanceY(g3,g-1) = 26
    c: Vertical(g4)
FEATURE [PartDesign::Pad] Pad004
  Direction = (1,0,0)
  Length = 5
  Length2 = 10
  Placement = pos=(0,0,0) rot=(0.57735,0.57735,0.57735;2.0944rad)
  Profile = -> Sketch006
  ReferenceAxis = -> Sketch006 [N_Axis]
  Reversed = true
  Type = 0
FEATURE [PartDesign::Plane] DatumPlane003
  Length = 60
  MapMode = 5
  Placement = pos=(2.9e-15,0,-26) rot=(0.707107,0.707107,0;3.14159rad)
  ResizeMode = 0
  Support = -> [Pad004]
  Width = 60
FEATURE [Sketcher::SketchObject] Sketch008
  FullyConstrained = true
  MapMode = 5
  Placement = pos=(2.9e-15,0,-26) rot=(0.707107,0.707107,0;3.14159rad)
  Support = -> [DatumPlane003]
  sketch-geometry (1):
    g0: Circle CenterX=0 CenterY=0 CenterZ=0 NormalX=0 NormalY=0 NormalZ=1 AngleXU=0 Radius=5
  constraints (2):
    c: Coincident(g0,g-1)
    c: Diameter(g0) = 10
FEATURE [PartDesign::Pad] Pad005
  BaseFeature = -> Pad004
  Direction = (0,0,-1)
  Length = 42
  Length2 = 10
  Placement = pos=(0,0,0) rot=(0.57735,0.57735,0.57735;2.0944rad)
  Profile = -> Sketch008
  ReferenceAxis = -> Sketch008 [N_Axis]
  Refine = true
  Reversed = true
  Type = 1
FEATURE [PartDesign::PolarPattern] PolarPattern002
  Angle = 360
  Axis = -> Z_Axis003
  BaseFeature = -> Pad005
  Mode = 0
  Occurrences = 3
  Offset = 120
  Originals = -> [Pad004]
  Placement = pos=(0,0,0) rot=(0.57735,0.57735,0.57735;2.0944rad)
  Refine = true
FEATURE [PartDesign::Body] Body002  label="base-skeleton"
  Group = -> [DatumPlane002,Sketch006,Pad004,DatumPlane003,Sketch008,Pad005,PolarPattern002]
  Origin = -> Origin003
  Tip = -> PolarPattern002
FEATURE [App::Part] Part  label="base"
  Group = -> [Body002,Body001]
  Origin = -> Origin
---- part cone.FCStd = doc fcstd_c84bd6ce8fa1 ----
FCSTD DOCUMENT  (FreeCAD 0.22R35451 (Git))
Label: cone
License: All rights reserved
LicenseURL: http://en.wikipedia.org/wiki/All_rights_reserved
objects: Sketcher::SketchObject×1, PartDesign::Revolution×1, PartDesign::Body×1, App::Part×1
note: 4 computed .brp shape members not serialized (recipe doc carries the construction recipe); baked Part::Feature solids carry a one-line shape summary decoded from their .brp

FEATURE [Sketcher::SketchObject] Sketch
  FullyConstrained = true
  MapMode = 5
  Placement = pos=(0,0,0) rot=(1,0,0;1.5708rad)
  Support = -> [XZ_Plane001]
  sketch-geometry (4):
    g0: LineSegment StartX=0 StartY=0 StartZ=0 EndX=0 EndY=20 EndZ=0
    g1: LineSegment StartX=0 StartY=20 StartZ=0 EndX=2 EndY=20 EndZ=0
    g2: ArcOfCircle CenterX=31 CenterY=20 CenterZ=0 NormalX=0 NormalY=0 NormalZ=1 AngleXU=0 Radius=29 StartAngle=3.14159 EndAngle=3.90261
    g3: LineSegment StartX=10 StartY=0 StartZ=0 EndX=0 EndY=0 EndZ=0
  constraints (11):
    c: Coincident(g-1,g0)
    c: PointOnObject(g0,g-2)
    c: Coincident(g0,g1)
    c: Horizontal(g1)
    c: Perpendicular(g1,g2) = 4.71239
    c: PointOnObject(g2,g-1)
    c: Coincident(g2,g3)
    c: Coincident(g3,g0)
    c: DistanceX(g1,g1) = 2
    c: DistanceX(g3,g3) = 10
    c: DistanceY(g0,g0) = 20
FEATURE [PartDesign::Revolution] Revolution
  Angle = 360
  Angle2 = 60
  Axis = (0,2e-16,1)
  Base = (0,0,0)
  Placement = pos=(0,0,0) rot=(1,0,0;1.5708rad)
  Profile = -> Sketch
  ReferenceAxis = -> Sketch [V_Axis]
  Refine = true
  Reversed = true
  Type = 0
FEATURE [PartDesign::Body] Body  label="cone0"
  Group = -> [Sketch,Revolution]
  Origin = -> Origin001
  Tip = -> Revolution
FEATURE [App::Part] Part  label="cone"
  Group = -> [Body]
  Origin = -> Origin
---- part link.FCStd = doc fcstd_2a591de467ad ----
FCSTD DOCUMENT  (FreeCAD 0.22R35451 (Git))
Label: link
License: All rights reserved
LicenseURL: http://en.wikipedia.org/wiki/All_rights_reserved
objects: Sketcher::SketchObject×5, PartDesign::Pad×2, PartDesign::Groove×2, PartDesign::Mirrored×2, PartDesign::Body×2, PartDesign::Pocket×1, PartDesign::Fillet×1, App::Part×1
note: 21 computed .brp shape members not serialized (recipe doc carries the construction recipe); baked Part::Feature solids carry a one-line shape summary decoded from their .brp

FEATURE [Sketcher::SketchObject] Sketch
  FullyConstrained = true
  MapMode = 5
  Support = -> [XY_Plane001]
  sketch-geometry (4):
    g0: ArcOfCircle CenterX=-70 CenterY=0 CenterZ=0 NormalX=0 NormalY=0 NormalZ=1 AngleXU=0 Radius=8 StartAngle=0.384397 EndAngle=5.89879
    g1: ArcOfCircle CenterX=70 CenterY=0 CenterZ=0 NormalX=0 NormalY=0 NormalZ=1 AngleXU=0 Radius=8 StartAngle=3.52599 EndAngle=9.04038
    g2: LineSegment StartX=-62.5838 StartY=-3 StartZ=0 EndX=62.5838 EndY=-3 EndZ=0
    g3: LineSegment StartX=62.5838 StartY=3 StartZ=0 EndX=-62.5838 EndY=3 EndZ=0
  constraints (13):
    c: PointOnObject(g0,g-1)
    c: Symmetric(g0,g1,g-1)
    c: Equal(g0,g1)
    c: DistanceX(g0,g1) = 140
    c: Horizontal(g2)
    c: Horizontal(g3)
    c: Coincident(g0,g3)
    c: Coincident(g1,g2)
    c: Coincident(g2,g0)
    c: Vertical(g0,g0)
    c: Radius(g0) = 8
    c: Distance(g0,g0) = 6
    c: Coincident(g1,g3)
FEATURE [PartDesign::Pad] Pad
  Direction = (0,0,1)
  Length = 6
  Length2 = 4
  Midplane = true
  Profile = -> Sketch
  ReferenceAxis = -> Sketch [N_Axis]
  Refine = true
  Type = 4
FEATURE [Sketcher::SketchObject] Sketch001
  FullyConstrained = true
  MapMode = 5
  Placement = pos=(0,0,0) rot=(1,0,0;1.5708rad)
  Support = -> [XZ_Plane001]
  sketch-geometry (4):
    g0: ArcOfCircle CenterX=-70 CenterY=0 CenterZ=0 NormalX=0 NormalY=0 NormalZ=1 AngleXU=0 Radius=5 StartAngle=1.5708 EndAngle=3.54431
    g1: LineSegment StartX=-74.6 StartY=-1.95959 StartZ=0 EndX=-79.2421 EndY=-10 EndZ=0
    g2: LineSegment StartX=-79.2421 StartY=-10 StartZ=0 EndX=-70 EndY=-10 EndZ=0
    g3: LineSegment StartX=-70 StartY=5 StartZ=0 EndX=-70 EndY=-10 EndZ=0
  constraints (13):
    c: Coincident(g1,g2)
    c: Horizontal(g2)
    c: PointOnObject(g0,g-1)
    c: Coincident(g3,g0)
    c: Coincident(g3,g2)
    c: Vertical(g3)
    c: PointOnObject(g0,g3)
    c: Radius(g0) = 5
    c: DistanceX(g0,g2) = 4.6
    c: DistanceX(g0,g-1) = 70
    c: Angle(g1,g3) = 0.523599
    c: DistanceY(g3,g3) = 15
    c: Coincident(g1,g0)
FEATURE [PartDesign::Groove] Groove
  Angle = 360
  Angle2 = 60
  Axis = (0,-2e-16,-1)
  Base = (-70,1.1e-15,5)
  BaseFeature = -> Pad
  Profile = -> Sketch001
  ReferenceAxis = -> Sketch001 [Edge4]
  Refine = true
  Reversed = true
  Type = 0
FEATURE [Sketcher::SketchObject] Sketch003
  FullyConstrained = true
  MapMode = 5
  Support = -> [XY_Plane002]
  sketch-geometry (4):
    g0: ArcOfCircle CenterX=-70 CenterY=0 CenterZ=0 NormalX=0 NormalY=0 NormalZ=1 AngleXU=0 Radius=8 StartAngle=0.384397 EndAngle=5.89879
    g1: ArcOfCircle CenterX=70 CenterY=0 CenterZ=0 NormalX=0 NormalY=0 NormalZ=1 AngleXU=0 Radius=8 StartAngle=3.52599 EndAngle=9.04038
    g2: LineSegment StartX=-62.5838 StartY=-3 StartZ=0 EndX=62.5838 EndY=-3 EndZ=0
    g3: LineSegment StartX=62.5838 StartY=3 StartZ=0 EndX=-62.5838 EndY=3 EndZ=0
  constraints (13):
    c: PointOnObject(g0,g-1)
    c: Symmetric(g0,g1,g-1)
    c: Equal(g0,g1)
    c: DistanceX(g0,g1) = 140
    c: Horizontal(g2)
    c: Horizontal(g3)
    c: Coincident(g0,g3)
    c: Coincident(g1,g2)
    c: Coincident(g2,g0)
    c: Vertical(g0,g0)
    c: Radius(g0) = 8
    c: Distance(g0,g0) = 6
    c: Coincident(g1,g3)
FEATURE [PartDesign::Pad] Pad001
  Direction = (0,0,1)
  Length = 6
  Length2 = 4
  Midplane = true
  Profile = -> Sketch003
  ReferenceAxis = -> Sketch003 [N_Axis]
  Refine = true
  Type = 4
FEATURE [Sketcher::SketchObject] Sketch004
  FullyConstrained = true
  MapMode = 5
  Placement = pos=(0,0,0) rot=(1,0,0;1.5708rad)
  Support = -> [XZ_Plane001]
  sketch-geometry (4):
    g0: ArcOfCircle CenterX=-70 CenterY=0 CenterZ=0 NormalX=0 NormalY=0 NormalZ=1 AngleXU=0 Radius=5 StartAngle=1.5708 EndAngle=3.54431
    g1: LineSegment StartX=-74.6 StartY=-1.95959 StartZ=0 EndX=-79.2421 EndY=-10 EndZ=0
    g2: LineSegment StartX=-79.2421 StartY=-10 StartZ=0 EndX=-70 EndY=-10 EndZ=0
    g3: LineSegment StartX=-70 StartY=5 StartZ=0 EndX=-70 EndY=-10 EndZ=0
  constraints (13):
    c: Coincident(g1,g2)
    c: Horizontal(g2)
    c: PointOnObject(g0,g-1)
    c: Coincident(g3,g0)
    c: Coincident(g3,g2)
    c: Vertical(g3)
    c: PointOnObject(g0,g3)
    c: Radius(g0) = 5
    c: DistanceX(g0,g2) = 4.6
    c: DistanceX(g0,g-1) = 70
    c: Angle(g1,g3) = 0.523599
    c: DistanceY(g3,g3) = 15
    c: Coincident(g1,g0)
FEATURE [PartDesign::Groove] Groove001
  Angle = 360
  Angle2 = 60
  Axis = (0,-2e-16,-1)
  Base = (-70,1.1e-15,5)
  BaseFeature = -> Pad001
  Profile = -> Sketch004
  ReferenceAxis = -> Sketch004 [Edge4]
  Refine = true
  Reversed = true
  Type = 0
FEATURE [Sketcher::SketchObject] Sketch005
  ExternalGeometry = -> [Sketch004]
  FullyConstrained = true
  MapMode = 5
  Placement = pos=(0,0,-4) rot=(1,0,0;3.14159rad)
  Support = -> [Groove001]
  sketch-geometry (4):
    g0: LineSegment StartX=-71 StartY=0.5 StartZ=0 EndX=-81 EndY=0.5 EndZ=0
    g1: LineSegment StartX=-81 StartY=0.5 StartZ=0 EndX=-81 EndY=-0.5 EndZ=0
    g2: LineSegment StartX=-81 StartY=-0.5 StartZ=0 EndX=-71 EndY=-0.5 EndZ=0
    g3: LineSegment StartX=-71 StartY=-0.5 StartZ=0 EndX=-71 EndY=0.5 EndZ=0
  constraints (11):
    c: Coincident(g0,g1)
    c: Coincident(g1,g2)
    c: Coincident(g2,g3)
    c: Coincident(g3,g0)
    c: Horizontal(g0)
    c: Horizontal(g2)
    c: Vertical(g1)
    c: Symmetric(g2,g0,g-1)
    c: Distance(g3,g3) = 1
    c: DistanceX(g2,g-3) = 1
    c: DistanceX(g2,g2) = 10
FEATURE [PartDesign::Pocket] Pocket
  BaseFeature = -> Groove001
  Direction = (0,0,1)
  Length = 8
  Length2 = 5
  Profile = -> Sketch005
  ReferenceAxis = -> Sketch005 [N_Axis]
  Refine = true
  Type = 0
FEATURE [PartDesign::Mirrored] Mirrored
  BaseFeature = -> Groove
  MirrorPlane = -> Sketch001 [V_Axis]
  Originals = -> [Groove]
  Refine = true
FEATURE [PartDesign::Body] Body  label="link-skel"
  Group = -> [Sketch,Pad,Sketch001,Groove,Mirrored]
  Origin = -> Origin001
  Tip = -> Mirrored
FEATURE [PartDesign::Mirrored] Mirrored001
  BaseFeature = -> Pocket
  MirrorPlane = -> Sketch005 [V_Axis]
  Originals = -> [Pocket,Groove001]
  Refine = true
FEATURE [PartDesign::Fillet] Fillet
  Base = -> Mirrored001 [Edge6,Edge8,Edge31,Edge27]
  BaseFeature = -> Mirrored001
  Radius = 10
  Refine = true
  SupportTransform = false
  UseAllEdges = false
FEATURE [PartDesign::Body] Body001  label="link0"
  Group = -> [Sketch003,Pad001,Sketch004,Groove001,Sketch005,Pocket,Mirrored001,Fillet]
  Origin = -> Origin002
  Tip = -> Fillet
FEATURE [App::Part] Part  label="link"
  Group = -> [Body,Body001]
  Origin = -> Origin
---- part nema17-48.FCStd = doc fcstd_b35fc45cbd58 ----
FCSTD DOCUMENT  (FreeCAD 0.22R35451 (Git))
Label: nema17-48
License: All rights reserved
LicenseURL: http://en.wikipedia.org/wiki/All_rights_reserved
objects: Sketcher::SketchObject×4, PartDesign::Pad×3, PartDesign::Chamfer×2, PartDesign::Hole×1, PartDesign::Body×1, App::Part×1
note: 17 computed .brp shape members not serialized (recipe doc carries the construction recipe); baked Part::Feature solids carry a one-line shape summary decoded from their .brp

FEATURE [Sketcher::SketchObject] Sketch
  FullyConstrained = false
  MapMode = 5
  Support = -> [XY_Plane]
  sketch-geometry (5):
    g0: LineSegment StartX=21.15 StartY=21.15 StartZ=0 EndX=-21.15 EndY=21.15 EndZ=0
    g1: LineSegment StartX=-21.15 StartY=21.15 StartZ=0 EndX=-21.15 EndY=-21.15 EndZ=0
    g2: LineSegment StartX=-21.15 StartY=-21.15 StartZ=0 EndX=21.15 EndY=-21.15 EndZ=0
    g3: LineSegment StartX=21.15 StartY=-21.15 StartZ=0 EndX=21.15 EndY=21.15 EndZ=0
    g4: Circle CenterX=0 CenterY=0 CenterZ=0 NormalX=0 NormalY=0 NormalZ=1 AngleXU=0 Radius=29.9106
  constraints (14):
    c: Coincident(g0,g1)
    c: Coincident(g1,g2)
    c: Coincident(g2,g3)
    c: Coincident(g3,g0)
    c: Equal(g0,g1)
    c: Equal(g0,g2)
    c: Equal(g0,g3)
    c: PointOnObject(g0,g4)
    c: PointOnObject(g1,g4)
    c: PointOnObject(g2,g4)
    c: PointOnObject(g3,g4)
    c: Coincident(g4,g-1)
    c: Horizontal(g0)
    c: DistanceY(g3,g3) = 42.3
FEATURE [PartDesign::Pad] Pad
  Direction = (0,0,1)
  Length = 48
  Length2 = 100
  Profile = -> Sketch
  ReferenceAxis = -> Sketch [N_Axis]
  Type = 0
FEATURE [Sketcher::SketchObject] Sketch001
  FullyConstrained = true
  MapMode = 5
  Placement = pos=(0,0,48) rot=(0,0,1;0rad)
  Support = -> [Pad]
  sketch-geometry (1):
    g0: Circle CenterX=0 CenterY=0 CenterZ=0 NormalX=0 NormalY=0 NormalZ=1 AngleXU=0 Radius=11
  constraints (2):
    c: Coincident(g0,g-1)
    c: Diameter(g0) = 22
FEATURE [PartDesign::Pad] Pad001
  BaseFeature = -> Pad
  Direction = (0,0,1)
  Length = 2
  Length2 = 100
  Profile = -> Sketch001
  ReferenceAxis = -> Sketch001 [N_Axis]
  Type = 0
FEATURE [Sketcher::SketchObject] Sketch002
  FullyConstrained = true
  MapMode = 5
  Placement = pos=(0,0,48) rot=(0,0,1;0rad)
  Support = -> [Pad001]
  sketch-geometry (1):
    g0: Circle CenterX=0 CenterY=0 CenterZ=0 NormalX=0 NormalY=0 NormalZ=1 AngleXU=0 Radius=2.5
  constraints (2):
    c: Coincident(g0,g-1)
    c: Diameter(g0) = 5
FEATURE [PartDesign::Pad] Pad002
  BaseFeature = -> Pad001
  Direction = (0,0,1)
  Length = 24
  Length2 = 100
  Profile = -> Sketch002
  ReferenceAxis = -> Sketch002 [N_Axis]
  Type = 0
FEATURE [PartDesign::Chamfer] Chamfer
  Angle = 45
  Base = -> Pad002 [Edge18]
  BaseFeature = -> Pad002
  ChamferType = 0
  FlipDirection = false
  Size = 0.5
  Size2 = 1
  SupportTransform = true
  UseAllEdges = false
FEATURE [Sketcher::SketchObject] Sketch004
  FullyConstrained = true
  MapMode = 5
  Placement = pos=(0,0,48) rot=(0,0,1;0rad)
  sketch-geometry (4):
    g0: Circle CenterX=15.5 CenterY=-15.5 CenterZ=0 NormalX=0 NormalY=0 NormalZ=1 AngleXU=0 Radius=1.25
    g1: Circle CenterX=15.5 CenterY=15.5 CenterZ=0 NormalX=0 NormalY=0 NormalZ=1 AngleXU=0 Radius=1.25
    g2: Circle CenterX=-15.5 CenterY=15.5 CenterZ=0 NormalX=0 NormalY=0 NormalZ=1 AngleXU=0 Radius=1.25
    g3: Circle CenterX=-15.5 CenterY=-15.5 CenterZ=0 NormalX=0 NormalY=0 NormalZ=1 AngleXU=0 Radius=1.25
  constraints (9):
    c: Diameter(g0) = 2.5
    c: Symmetric(g1,g0,g-1)
    c: Symmetric(g1,g2,g-2)
    c: Symmetric(g3,g2,g-1)
    c: Equal(g2,g1)
    c: Equal(g1,g3)
    c: Equal(g3,g0)
    c: DistanceX(g2,g1) = 31
    c: DistanceY(g0,g1) = 31
FEATURE [PartDesign::Hole] Hole
  BaseFeature = -> Chamfer
  CustomThreadClearance = 0
  Depth = 4
  DepthType = 0
  Diameter = 3.4
  DrillForDepth = false
  DrillPoint = 1
  DrillPointAngle = 118
  HoleCutCountersinkAngle = 90
  HoleCutCustomValues = false
  HoleCutDepth = 0
  HoleCutDiameter = 1.6
  HoleCutType = 0
  ModelThread = false
  Profile = -> Sketch004
  Tapered = false
  TaperedAngle = 90
  ThreadClass = 0
  ThreadDepth = 4
  ThreadDepthType = 0
  ThreadDirection = 0
  ThreadFit = 0
  ThreadSize = 9
  ThreadType = 1
  Threaded = false
  UseCustomThreadClearance = false
FEATURE [PartDesign::Chamfer] Chamfer001
  Angle = 45
  Base = -> Hole [Edge20,Edge17,Edge22,Edge18]
  BaseFeature = -> Hole
  ChamferType = 0
  FlipDirection = false
  Size = 5
  Size2 = 1
  SupportTransform = true
  UseAllEdges = false
FEATURE [PartDesign::Body] Body  label="nema17"
  Group = -> [Sketch,Pad,Sketch001,Pad001,Sketch002,Pad002,Chamfer,Sketch004,Hole,Chamfer001]
  Origin = -> Origin
  Placement = pos=(0,0,-50) rot=(0,0,1;0rad)
  Tip = -> Chamfer001
FEATURE [App::Part] Part  label="nema17-48"
  Group = -> [Body]
  Origin = -> Origin001
---- part plate.FCStd = doc fcstd_dd23bfd2ac05 ----
FCSTD DOCUMENT  (FreeCAD 2024.1R35694 (Git))
Label: plate
License: All rights reserved
LicenseURL: http://en.wikipedia.org/wiki/All_rights_reserved
objects: Sketcher::SketchObject×6, PartDesign::PolarPattern×3, PartDesign::Pad×2, PartDesign::Revolution×2, PartDesign::Body×2, PartDesign::Chamfer×2, PartDesign::Pocket×2, App::Part×1
note: 27 computed .brp shape members not serialized (recipe doc carries the construction recipe); baked Part::Feature solids carry a one-line shape summary decoded from their .brp

FEATURE [Sketcher::SketchObject] Sketch003
  FullyConstrained = true
  MapMode = 5
  Support = -> [XY_Plane002]
  sketch-geometry (4):
    g0: LineSegment StartX=19 StartY=0 StartZ=0 EndX=19 EndY=50 EndZ=0
    g1: LineSegment StartX=19 StartY=50 StartZ=0 EndX=-19 EndY=50 EndZ=0
    g2: LineSegment StartX=-19 StartY=50 StartZ=0 EndX=-19 EndY=0 EndZ=0
    g3: LineSegment StartX=-19 StartY=0 StartZ=0 EndX=19 EndY=0 EndZ=0
  constraints (11):
    c: Coincident(g0,g1)
    c: Coincident(g1,g2)
    c: Coincident(g2,g3)
    c: Coincident(g3,g0)
    c: Vertical(g0)
    c: Vertical(g2)
    c: Horizontal(g1)
    c: PointOnObject(g0,g-1)
    c: Symmetric(g2,g0,g-2)
    c: DistanceX(g3,g3) = 38
    c: DistanceY(g0,g0) = 50
FEATURE [PartDesign::Pad] Pad001
  Direction = (0,0,1)
  Length = 6
  Length2 = 10
  Profile = -> Sketch003
  ReferenceAxis = -> Sketch003 [N_Axis]
  Type = 0
FEATURE [Sketcher::SketchObject] Sketch
  ExternalGeometry = -> [Pad001]
  FullyConstrained = true
  MapMode = 5
  Support = -> [XY_Plane002]
  sketch-geometry (4):
    g0: LineSegment StartX=-30 StartY=50 StartZ=0 EndX=30 EndY=50 EndZ=0
    g1: ArcOfCircle CenterX=-25 CenterY=50 CenterZ=0 NormalX=0 NormalY=0 NormalZ=1 AngleXU=0 Radius=5 StartAngle=0.643501 EndAngle=3.14159
    g2: ArcOfCircle CenterX=25 CenterY=50 CenterZ=0 NormalX=0 NormalY=0 NormalZ=1 AngleXU=0 Radius=5 StartAngle=-9e-16 EndAngle=2.49809
    g3: LineSegment StartX=-21 StartY=53 StartZ=0 EndX=21 EndY=53 EndZ=0
  constraints (12):
    c: Symmetric(g0,g0,g-2)
    c: PointOnObject(g-3,g0)
    c: PointOnObject(g1,g0)
    c: Coincident(g1,g0)
    c: Coincident(g2,g0)
    c: Symmetric(g1,g2,g-2)
    c: DistanceX(g1,g2) = 50
    c: Radius(g1) = 5
    c: Coincident(g3,g1)
    c: Coincident(g3,g2)
    c: Horizontal(g3)
    c: DistanceY(g-3,g1) = 3
FEATURE [PartDesign::Revolution] Revolution
  Angle = 360
  Angle2 = 60
  Axis = (1,-1e-16,0)
  Base = (-30,50,0)
  BaseFeature = -> Pad001
  Profile = -> Sketch
  ReferenceAxis = -> Sketch [Edge1]
  Refine = true
  Type = 0
FEATURE [PartDesign::PolarPattern] PolarPattern
  Angle = 360
  Axis = -> Sketch003 [N_Axis]
  BaseFeature = -> Revolution
  Mode = 0
  Occurrences = 3
  Offset = 120
  Originals = -> [Pad001,Revolution]
  Refine = true
FEATURE [PartDesign::Body] Body001  label="plate-skel"
  Group = -> [Sketch003,Pad001,Sketch,Revolution,PolarPattern]
  Origin = -> Origin002
  Tip = -> PolarPattern
FEATURE [Sketcher::SketchObject] Sketch005
  FullyConstrained = true
  MapMode = 5
  Support = -> [XY_Plane003]
  sketch-geometry (4):
    g0: LineSegment StartX=15 StartY=0 StartZ=0 EndX=15 EndY=50 EndZ=0
    g1: LineSegment StartX=15 StartY=50 StartZ=0 EndX=-15 EndY=50 EndZ=0
    g2: LineSegment StartX=-15 StartY=50 StartZ=0 EndX=-15 EndY=0 EndZ=0
    g3: LineSegment StartX=-15 StartY=0 StartZ=0 EndX=15 EndY=0 EndZ=0
  constraints (11):
    c: Coincident(g0,g1)
    c: Coincident(g1,g2)
    c: Coincident(g2,g3)
    c: Coincident(g3,g0)
    c: Vertical(g0)
    c: Vertical(g2)
    c: Horizontal(g1)
    c: PointOnObject(g0,g-1)
    c: Symmetric(g2,g0,g-2)
    c: DistanceX(g3,g3) = 30
    c: DistanceY(g0,g0) = 50
FEATURE [PartDesign::Pad] Pad002
  Direction = (0,0,1)
  Length = 6
  Length2 = 10
  Profile = -> Sketch005
  ReferenceAxis = -> Sketch005 [N_Axis]
  Type = 0
FEATURE [Sketcher::SketchObject] Sketch004
  ExternalGeometry = -> [Pad002]
  FullyConstrained = true
  MapMode = 5
  Support = -> [XY_Plane003]
  sketch-geometry (4):
    g0: LineSegment StartX=-29.9 StartY=50 StartZ=0 EndX=29.9 EndY=50 EndZ=0
    g1: ArcOfCircle CenterX=-25 CenterY=50 CenterZ=0 NormalX=0 NormalY=0 NormalZ=1 AngleXU=0 Radius=4.9 StartAngle=0.658897 EndAngle=3.14159
    g2: ArcOfCircle CenterX=25 CenterY=50 CenterZ=0 NormalX=0 NormalY=0 NormalZ=1 AngleXU=0 Radius=4.9 StartAngle=4e-16 EndAngle=2.4827
    g3: LineSegment StartX=-21.1257 StartY=53 StartZ=0 EndX=21.1257 EndY=53 EndZ=0
  constraints (12):
    c: Symmetric(g0,g0,g-2)
    c: PointOnObject(g-3,g0)
    c: PointOnObject(g1,g0)
    c: Coincident(g1,g0)
    c: Coincident(g2,g0)
    c: Symmetric(g1,g2,g-2)
    c: DistanceX(g1,g2) = 50
    c: Radius(g1) = 4.9
    c: Coincident(g3,g1)
    c: Coincident(g3,g2)
    c: Horizontal(g3)
    c: DistanceY(g-3,g1) = 3
FEATURE [PartDesign::Revolution] Revolution001
  Angle = 360
  Angle2 = 60
  Axis = (1,0,0)
  Base = (-29.9,50,0)
  BaseFeature = -> Pad002
  Profile = -> Sketch004
  ReferenceAxis = -> Sketch004 [Edge1]
  Refine = true
  Type = 0
FEATURE [PartDesign::PolarPattern] PolarPattern001
  Angle = 360
  Axis = -> Sketch005 [N_Axis]
  BaseFeature = -> Revolution001
  Mode = 0
  Occurrences = 3
  Offset = 120
  Originals = -> [Pad002,Revolution001]
  Refine = true
FEATURE [PartDesign::Chamfer] Chamfer
  Angle = 45
  Base = -> PolarPattern001 [Edge17,Edge44,Edge35]
  BaseFeature = -> PolarPattern001
  ChamferType = 0
  FlipDirection = false
  Refine = true
  Size = 2.4
  Size2 = 1
  SupportTransform = false
  UseAllEdges = false
FEATURE [Sketcher::SketchObject] Sketch006
  FullyConstrained = true
  MapMode = 5
  Placement = pos=(0,0,0) rot=(1,0,0;3.14159rad)
  Support = -> [Chamfer]
  sketch-geometry (7):
    g0: LineSegment StartX=25.9808 StartY=45 StartZ=0 EndX=-25.9808 EndY=45 EndZ=0
    g1: LineSegment StartX=-25.9808 StartY=45 StartZ=0 EndX=-51.9615 EndY=0 EndZ=0
    g2: LineSegment StartX=-51.9615 StartY=0 StartZ=0 EndX=-25.9808 EndY=-45 EndZ=0
    g3: LineSegment StartX=-25.9808 StartY=-45 StartZ=0 EndX=25.9808 EndY=-45 EndZ=0
    g4: LineSegment StartX=25.9808 StartY=-45 StartZ=0 EndX=51.9615 EndY=0 EndZ=0
    g5: LineSegment StartX=51.9615 StartY=0 StartZ=0 EndX=25.9808 EndY=45 EndZ=0
    g6: Circle CenterX=0 CenterY=0 CenterZ=0 NormalX=0 NormalY=0 NormalZ=1 AngleXU=0 Radius=51.9615
  constraints (16):
    c: Coincident(g0,g1)
    c: Coincident(g1,g2)
    c: Coincident(g2,g3)
    c: Coincident(g3,g4)
    c: Coincident(g4,g5)
    c: Coincident(g5,g0)
    c: Equal(g0, g1-g5) x5
    c: PointOnObject(g0,g6)
    c: PointOnObject(g1,g6)
    c: PointOnObject(g2,g6)
    c: PointOnObject(g3,g6)
    c: PointOnObject(g4,g6)
    c: PointOnObject(g5,g6)
    c: Coincident(g6,g-1)
    c: Horizontal(g0)
    c: DistanceY(g3,g0) = 90
FEATURE [PartDesign::Pocket] Pocket
  BaseFeature = -> Chamfer
  Direction = (0,0,1)
  Length = 3
  Length2 = 5
  Profile = -> Sketch006
  ReferenceAxis = -> Sketch006 [N_Axis]
  Refine = true
  Type = 0
FEATURE [Sketcher::SketchObject] Sketch007
  FullyConstrained = true
  MapMode = 5
  Placement = pos=(0,0,3) rot=(1,0,0;3.14159rad)
  Support = -> [Pocket]
  sketch-geometry (6):
    g0: Circle CenterX=-6.25 CenterY=-37.5 CenterZ=0 NormalX=0 NormalY=0 NormalZ=1 AngleXU=0 Radius=3.5
    g1: Circle CenterX=6.25 CenterY=-37.5 CenterZ=0 NormalX=0 NormalY=0 NormalZ=1 AngleXU=0 Radius=3.5
    g2: Circle CenterX=-6.25 CenterY=-25 CenterZ=0 NormalX=0 NormalY=0 NormalZ=1 AngleXU=0 Radius=3.5
    g3: Circle CenterX=6.25 CenterY=-25 CenterZ=0 NormalX=0 NormalY=0 NormalZ=1 AngleXU=0 Radius=3.5
    g4: Circle CenterX=6.25 CenterY=-12.5 CenterZ=0 NormalX=0 NormalY=0 NormalZ=1 AngleXU=0 Radius=3.5
    g5: Circle CenterX=-6.25 CenterY=-12.5 CenterZ=0 NormalX=0 NormalY=0 NormalZ=1 AngleXU=0 Radius=3.5
  constraints (15):
    c: Symmetric(g0,g1,g-2)
    c: Symmetric(g2,g3,g-2)
    c: DistanceX(g2,g3) = 12.5
    c: DistanceY(g1,g3) = 12.5
    c: Diameter(g3) = 7
    c: Equal(g2,g3)
    c: Equal(g0,g1)
    c: DistanceY(g3,g-1) = 25
    c: Vertical(g3,g1)
    c: Equal(g0,g2)
    c: Symmetric(g5,g4,g-2)
    c: Vertical(g2,g5)
    c: DistanceY(g3,g4) = 12.5
    c: Equal(g5,g2)
    c: Equal(g4,g5)
FEATURE [PartDesign::Pocket] Pocket001
  BaseFeature = -> Pocket
  Direction = (0,0,1)
  Length = 5
  Length2 = 5
  Profile = -> Sketch007
  ReferenceAxis = -> Sketch007 [N_Axis]
  Refine = true
  Type = 1
FEATURE [PartDesign::PolarPattern] PolarPattern002
  Angle = 360
  Axis = -> Z_Axis003
  BaseFeature = -> Pocket001
  Mode = 0
  Occurrences = 3
  Offset = 120
  Originals = -> [Pocket001]
  Refine = true
FEATURE [PartDesign::Chamfer] Chamfer001
  Angle = 45
  Base = -> PolarPattern002 [Edge68,Edge120,Edge121]
  BaseFeature = -> PolarPattern002
  ChamferType = 0
  FlipDirection = false
  Refine = true
  Size = 1
  Size2 = 1
  SupportTransform = false
  UseAllEdges = false
FEATURE [PartDesign::Body] Body002  label="plate-0"
  Group = -> [Sketch005,Pad002,Sketch004,Revolution001,PolarPattern001,Chamfer,Sketch006,Pocket,Sketch007,Pocket001,PolarPattern002,Chamfer001]
  Origin = -> Origin003
  Tip = -> Chamfer001
FEATURE [App::Part] Part  label="plate"
  Group = -> [Body001,Body002]
  Origin = -> Origin001
